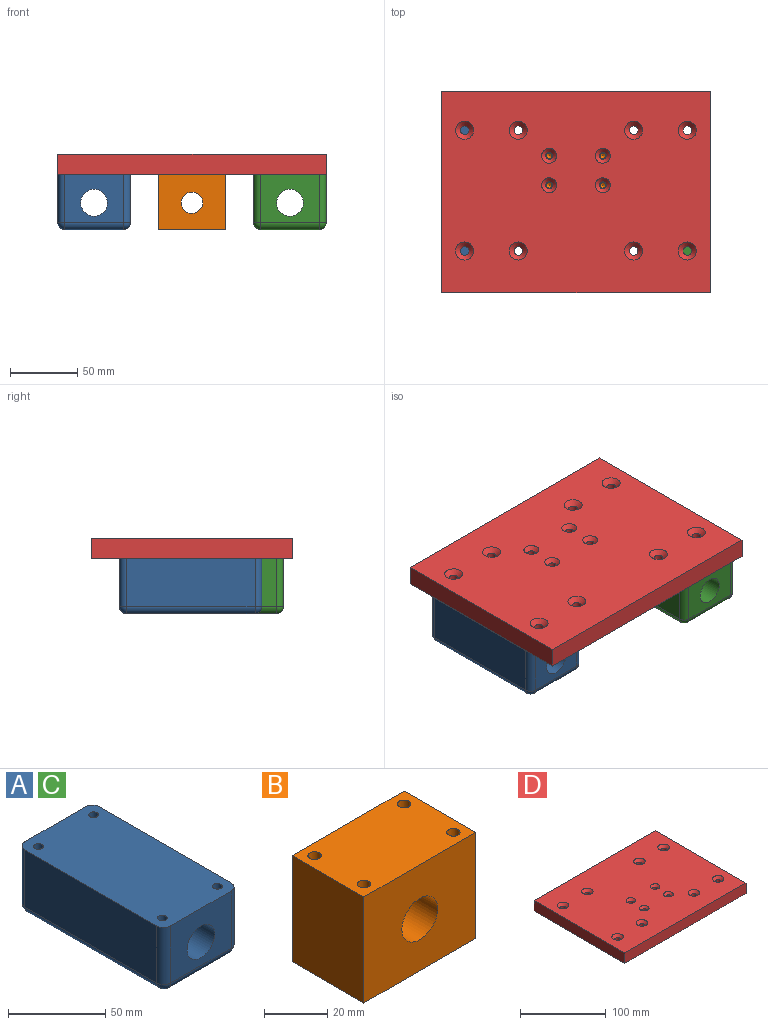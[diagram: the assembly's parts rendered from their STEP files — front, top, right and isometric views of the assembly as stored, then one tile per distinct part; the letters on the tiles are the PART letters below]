
ASSEMBLY  parts=4 mates=2
PART A: 23 faces, bbox 54x106x41 mm
  f0: plane 96x36mm, normal (1,0,0), area 3456mm2, adj f1,f11,f12,f13
  f1: plane 106x54mm, normal (0,0,1), area 5624mm2, adj f0,f2,f5,f6,f7,f8,f9,f10
  f2: plane 96x36mm, normal (-1,0,0), area 3456mm2, adj f1,f16,f19,f22
  f3: plane 96x44mm, normal (0,0,-1), area 4149.5mm2, adj f7,f8,f9,f10,f12,f17,f18,f22
  f4: cylinder r=10mm len=106mm, axis (0,1,0), area 6660.2mm2, adj f5,f6
  f5: plane 44x36mm, normal (0,-1,0), area 1269.8mm2, adj f1,f4,f11,f16,f17
  f6: plane 44x36mm, normal (0,1,0), area 1269.8mm2, adj f1,f4,f13,f18,f19
  f7: cylinder r=2.5mm len=41mm, axis (0,0,1), area 644mm2, adj f1,f3,f22
  f8: cylinder r=2.5mm len=41mm, axis (0,0,1), area 644mm2, adj f1,f3,f12
  f9: cylinder r=2.5mm len=41mm, axis (0,0,1), area 644mm2, adj f1,f3,f22
  f10: cylinder r=2.5mm len=41mm, axis (0,0,1), area 644mm2, adj f1,f3,f12
  f11: cylinder r=5mm len=36mm, axis (0,0,-1), area 282.7mm2, adj f0,f1,f5,f14
  f12: cylinder r=5mm len=96mm, axis (0,1,0), area 751.9mm2, adj f0,f3,f8,f10,f14,f15
  f13: cylinder r=5mm len=36mm, axis (0,0,1), area 282.7mm2, adj f0,f1,f6,f15
  f14: sphere r=5mm, area 39.3mm2, adj f11,f12,f17
  f15: sphere r=5mm, area 39.3mm2, adj f12,f13,f18
  f16: cylinder r=5mm len=36mm, axis (0,0,1), area 282.7mm2, adj f1,f2,f5,f20
  f17: cylinder r=5mm len=44mm, axis (-1,0,0), area 345.6mm2, adj f3,f5,f14,f20
  f18: cylinder r=5mm len=44mm, axis (1,0,0), area 345.6mm2, adj f3,f6,f15,f21
  f19: cylinder r=5mm len=36mm, axis (0,0,-1), area 282.7mm2, adj f1,f2,f6,f21
  f20: sphere r=5mm, area 39.3mm2, adj f16,f17,f22
  f21: sphere r=5mm, area 39.3mm2, adj f18,f19,f22
  f22: cylinder r=5mm len=96mm, axis (0,-1,0), area 751.9mm2, adj f2,f3,f7,f9,f20,f21
PART B: 15 faces, bbox 50x32x41 mm
  f0: plane 50x32mm, normal (0,0,-1), area 1600mm2, adj f1,f4,f5,f6
  f1: plane 41x32mm, normal (1,0,0), area 1312mm2, adj f0,f2,f5,f6
  f2: plane 50x32mm, normal (0,0,1), area 1544.6mm2, adj f1,f4,f5,f6,f7,f9,f11,f13
  f3: cylinder r=8mm len=32mm, axis (0,1,0), area 1608.5mm2, adj f5,f6
  f4: plane 41x32mm, normal (-1,0,0), area 1312mm2, adj f0,f2,f5,f6
  f5: plane 50x41mm, normal (0,-1,0), area 1848.9mm2, adj f0,f1,f2,f3,f4
  f6: plane 50x41mm, normal (0,1,0), area 1848.9mm2, adj f0,f1,f2,f3,f4
  f7: cylinder r=2.1mm len=14.4mm, axis (0,0,1), area 190mm2, adj f2,f8
  f8: cone r=0mm half-angle=59deg, axis (0,0,1), area 16.2mm2, adj f7
  f9: cylinder r=2.1mm len=14.4mm, axis (0,0,1), area 190mm2, adj f2,f10
  f10: cone r=0mm half-angle=59deg, axis (0,0,1), area 16.2mm2, adj f9
  f11: cylinder r=2.1mm len=14.4mm, axis (0,0,1), area 190mm2, adj f2,f12
  f12: cone r=0mm half-angle=59deg, axis (0,0,1), area 16.2mm2, adj f11
  f13: cylinder r=2.1mm len=14.4mm, axis (0,0,1), area 190mm2, adj f2,f14
  f14: cone r=0mm half-angle=59deg, axis (0,0,1), area 16.2mm2, adj f13
PART C: same geometry as A
PART D: 30 faces, bbox 200x150x15 mm
  f0: plane 150x15mm, normal (1,0,0), area 2250mm2, adj f1,f3,f4,f5
  f1: plane 200x15mm, normal (0,1,0), area 3000mm2, adj f0,f2,f4,f5
  f2: plane 150x15mm, normal (-1,0,0), area 2250mm2, adj f1,f3,f4,f5
  f3: plane 200x15mm, normal (0,-1,0), area 3000mm2, adj f0,f2,f4,f5
  f4: plane 200x150mm, normal (0,0,1), area 28471mm2, adj f0,f1,f2,f3,f7,f9,f11,f13
  f5: plane 200x150mm, normal (0,0,-1), area 29631.3mm2, adj f0,f1,f2,f3,f6,f8,f10,f12
  f6: cylinder r=3.3mm len=11.58mm, axis (0,0,1), area 240.1mm2, adj f5,f7
  f7: cone r=3.3mm half-angle=45deg, axis (0,0,1), area 152.3mm2, adj f4,f6
  f8: cylinder r=3.3mm len=11.58mm, axis (0,0,1), area 240.1mm2, adj f5,f9
  f9: cone r=3.3mm half-angle=45deg, axis (0,0,1), area 152.3mm2, adj f4,f8
  f10: cylinder r=3.3mm len=11.58mm, axis (0,0,1), area 240.1mm2, adj f5,f11
  f11: cone r=3.3mm half-angle=45deg, axis (0,0,1), area 152.3mm2, adj f4,f10
  f12: cylinder r=3.3mm len=11.58mm, axis (0,0,1), area 240.1mm2, adj f5,f13
  f13: cone r=3.3mm half-angle=45deg, axis (0,0,1), area 152.3mm2, adj f4,f12
  f14: cylinder r=3.3mm len=11.58mm, axis (0,0,1), area 240.1mm2, adj f5,f15
  f15: cone r=3.3mm half-angle=45deg, axis (0,0,1), area 152.3mm2, adj f4,f14
  f16: cylinder r=3.3mm len=11.58mm, axis (0,0,1), area 240.1mm2, adj f5,f17
  f17: cone r=3.3mm half-angle=45deg, axis (0,0,1), area 152.3mm2, adj f4,f16
  f18: cylinder r=3.3mm len=11.58mm, axis (0,0,1), area 240.1mm2, adj f5,f19
  f19: cone r=3.3mm half-angle=45deg, axis (0,0,1), area 152.3mm2, adj f4,f18
  f20: cylinder r=3.3mm len=11.58mm, axis (0,0,1), area 240.1mm2, adj f5,f21
  f21: cone r=3.3mm half-angle=45deg, axis (0,0,1), area 152.3mm2, adj f4,f20
  f22: cylinder r=2.75mm len=12.15mm, axis (0,0,1), area 209.9mm2, adj f5,f23
  f23: cone r=2.75mm half-angle=45deg, axis (0,0,1), area 105.7mm2, adj f4,f22
  f24: cylinder r=2.75mm len=12.15mm, axis (0,0,1), area 209.9mm2, adj f5,f25
  f25: cone r=2.75mm half-angle=45deg, axis (0,0,1), area 105.7mm2, adj f4,f24
  f26: cylinder r=2.75mm len=12.15mm, axis (0,0,1), area 209.9mm2, adj f5,f27
  f27: cone r=2.75mm half-angle=45deg, axis (0,0,1), area 105.7mm2, adj f4,f26
  f28: cylinder r=2.75mm len=12.15mm, axis (0,0,1), area 209.9mm2, adj f5,f29
  f29: cone r=2.75mm half-angle=45deg, axis (0,0,1), area 105.7mm2, adj f4,f28
PLACE A t=(-83.89,-31.42,14.65)mm
PLACE B t=(-10.89,-53.42,14.65)mm
PLACE C t=(62.11,-47.42,14.65)mm
PLACE D rot(axis=(0,0,1),180deg) t=(-10.89,-85.42,35.15)mm
MATE fastened D.f5 <-> A.f9  axis (0,0,-1) through (-103.89,-129.42,35.15)mm
MATE fastened B.f9 <-> D.f22  axis (0,0,1) through (9.11,-58.42,35.15)mm
